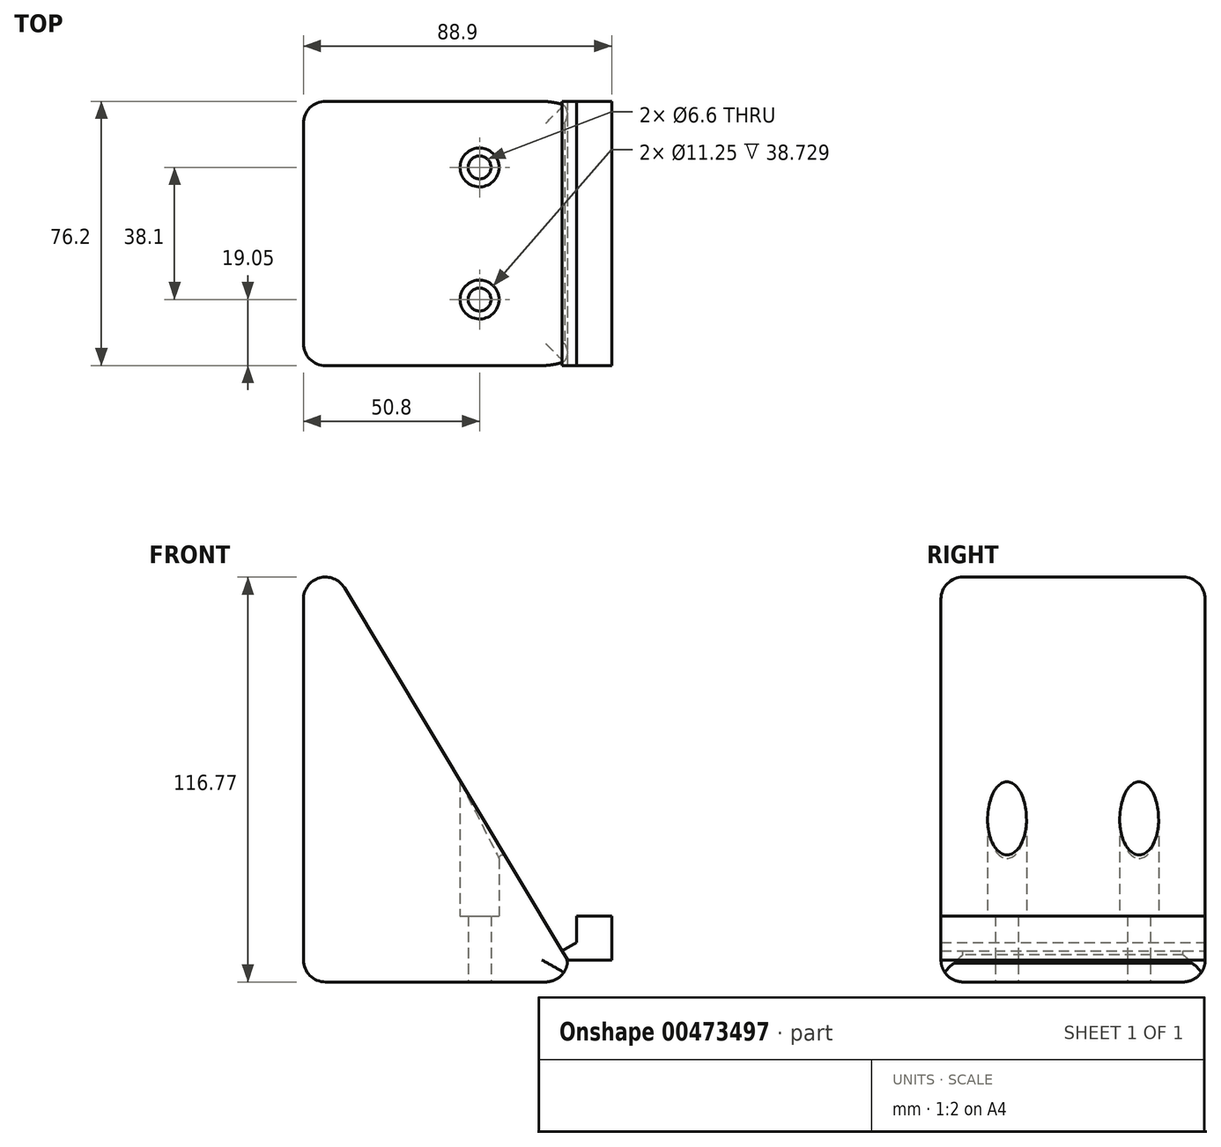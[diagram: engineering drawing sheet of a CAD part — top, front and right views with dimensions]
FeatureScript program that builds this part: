
annotation { "Feature Type Name" : "Feature", "Feature Type Description" : "" }
export const myFeature = defineFeature(function(context is Context, id is Id, definition is map)
    precondition{}
    {
        {
            var Q0;
            Q0=qCreatedBy(makeId("Top.planeOp"),FACE);
            var sketch = newSketch(context, id + "F0", { "sketchPlane" : qUnion([Q0])});
            skLineSegment(sketch, "E0.bottom", {"start": v(-38.1, 38.1) * mm, "end": v(38.1, 38.1) * mm});
            skLineSegment(sketch, "E0.top", {"start": v(-38.1, -38.1) * mm, "end": v(38.1, -38.1) * mm});
            skLineSegment(sketch, "E0.left", {"start": v(-38.1, 38.1) * mm, "end": v(-38.1, -38.1) * mm});
            skLineSegment(sketch, "E0.right", {"start": v(38.1, 38.1) * mm, "end": v(38.1, -38.1) * mm});
            skPoint(sketch, "E0.middle", {"position": v(0, 0) * mm});
            skSolve(sketch);
        }
        {
            var Q0;
            Q0=makeQuery(id+"F0.imprint","IMPRINT",FACE,{"disambiguationData":[TD([[makeQuery(id+"F0.imprint","IMPRINT",EDGE,{"derivedFrom":sQuery(id+"F0.wireOp",EDGE,"E0.bottom")}),-1.0]])]});
            extrude(context, id + "F1", {"entities" : qUnion([Q0]), "oppositeDirection" : true, "depth" : 6.35 * mm});
        }
        {
            var Q0;
            Q0=qCreatedBy(makeId("Front.planeOp"),FACE);
            var sketch = newSketch(context, id + "F2", { "sketchPlane" : qUnion([Q0])});
            skLineSegment(sketch, "E1", {"start": v(38.1, 0) * mm, "end": v(-38.1, 0) * mm});
            skLineSegment(sketch, "E2", {"start": v(38.1, 0) * mm, "end": v(-38.1, 127) * mm});
            skLineSegment(sketch, "E3", {"start": v(-38.1, 127) * mm, "end": v(-38.1, 0) * mm});
            skLineSegment(sketch, "E4", {"start": v(38.1, 0) * mm, "end": v(50.8, 0) * mm});
            skLineSegment(sketch, "E5", {"start": v(50.8, 0) * mm, "end": v(50.8, 12.7) * mm});
            skLineSegment(sketch, "E6", {"start": v(50.8, 12.7) * mm, "end": v(40.64, 12.7) * mm});
            skLineSegment(sketch, "E7", {"start": v(40.64, 12.7) * mm, "end": v(40.64, 5.08) * mm});
            skLineSegment(sketch, "E8", {"start": v(40.64, 5.08) * mm, "end": v(36.53, 2.61) * mm});
            skSolve(sketch);
        }
        {
            var Q0;
            Q0=makeQuery(id+"F2.imprint","IMPRINT",FACE,{"disambiguationData":[TD([[makeQuery(id+"F2.imprint","IMPRINT",EDGE,{"derivedFrom":sQuery(id+"F2.wireOp",EDGE,"E1")}),-1.0]])]});
            extrude(context, id + "F3", {"entities" : qUnion([Q0]), "operationType" : NewBodyOperationType.ADD, "depth" : 38.1 * mm, "hasSecondDirection" : true, "secondDirectionOppositeDirection" : true, "secondDirectionDepth" : 38.1 * mm});
        }
        {
            var Q0;
            Q0=makeQuery(id+"F3.opExtrude","SWEPT_FACE",FACE,{"disambiguationData":[OSD([sQuery(id+"F2.wireOp",EDGE,"E2")])]});
            var Q1;
            Q1=makeQuery(id+"F3.boolean.opBoolean","MERGE",FACE,{"derivedFrom":[makeQuery(id+"F1.opExtrude","SWEPT_FACE",FACE,{"disambiguationData":[OSD([sQuery(id+"F0.wireOp",EDGE,"E0.left")])]}),makeQuery(id+"F3.opExtrude","SWEPT_FACE",FACE,{"disambiguationData":[OSD([sQuery(id+"F2.wireOp",EDGE,"E3")])]})]});
            var Q2;
            Q2=makeQuery(id+"F1.opExtrude","CAP_FACE",FACE,{"disambiguationData":[OSD([sQuery(id+"F0.wireOp",EDGE,"E0.bottom"),sQuery(id+"F0.wireOp",EDGE,"E0.top"),sQuery(id+"F0.wireOp",EDGE,"E0.left"),sQuery(id+"F0.wireOp",EDGE,"E0.right")])],"isStart":false});
            fillet(context, id + "F4", {"entities" : qUnion([Q0, Q1, Q2]), "radius" : 6.35 * mm, "tangentPropagation" : true, "allowEdgeOverflow" : false});
        }
        {
            var Q0;
            Q0=makeQuery(id+"F1.opExtrude","CAP_FACE",FACE,{"disambiguationData":[OSD([sQuery(id+"F0.wireOp",EDGE,"E0.bottom"),sQuery(id+"F0.wireOp",EDGE,"E0.top"),sQuery(id+"F0.wireOp",EDGE,"E0.left"),sQuery(id+"F0.wireOp",EDGE,"E0.right")])],"isStart":false});
            var sketch = newSketch(context, id + "F5", { "sketchPlane" : qUnion([Q0])});
            skLineSegment(sketch, "E9", {"start": v(0, 0) * mm, "end": v(12.7, 0) * mm});
            skLineSegment(sketch, "E10", {"start": v(12.7, 0) * mm, "end": v(12.7, -19.05) * mm});
            skLineSegment(sketch, "E11", {"start": v(12.7, 0) * mm, "end": v(12.7, 19.05) * mm});
            skCircle(sketch, "E12", {"center": v(12.7, -19.05) * mm, "radius": 3.3 * mm});
            skCircle(sketch, "E13", {"center": v(12.7, 19.05) * mm, "radius": 3.3 * mm});
            skCircle(sketch, "E14", {"center": v(12.7, -19.05) * mm, "radius": 5.63 * mm});
            skCircle(sketch, "E15", {"center": v(12.7, 19.05) * mm, "radius": 5.63 * mm});
            skSolve(sketch);
        }
        {
            var Q0;
            Q0=makeQuery(id+"F5.imprint","IMPRINT",FACE,{"disambiguationData":[TD([[makeQuery(id+"F5.imprint","IMPRINT",EDGE,{"derivedFrom":sQuery(id+"F5.wireOp",EDGE,"E13")}),1.0]])]});
            var Q1;
            Q1=makeQuery(id+"F5.imprint","IMPRINT",FACE,{"disambiguationData":[TD([[makeQuery(id+"F5.imprint","IMPRINT",EDGE,{"derivedFrom":sQuery(id+"F5.wireOp",EDGE,"E12")}),1.0]])]});
            extrude(context, id + "F6", {"entities" : qUnion([Q0, Q1]), "operationType" : NewBodyOperationType.REMOVE, "endBound" : BoundingType.THROUGH_ALL, "oppositeDirection" : true, "depth" : 25.4 * mm});
        }
        {
            var Q0;
            Q0=makeQuery(id+"F5.imprint","IMPRINT",FACE,{"disambiguationData":[TD([[makeQuery(id+"F5.imprint","IMPRINT",EDGE,{"derivedFrom":sQuery(id+"F5.wireOp",EDGE,"E13")}),-1.0]])]});
            var Q1;
            Q1=makeQuery(id+"F5.imprint","IMPRINT",FACE,{"disambiguationData":[TD([[makeQuery(id+"F5.imprint","IMPRINT",EDGE,{"derivedFrom":sQuery(id+"F5.wireOp",EDGE,"E12")}),-1.0]])]});
            extrude(context, id + "F7", {"entities" : qUnion([Q0, Q1]), "operationType" : NewBodyOperationType.REMOVE, "endBound" : BoundingType.THROUGH_ALL, "oppositeDirection" : true, "depth" : 76.2 * mm, "hasSecondDirection" : true, "secondDirectionOppositeDirection" : true, "secondDirectionDepth" : 19.05 * mm});
        }
        {
            var Q0;
            Q0=makeQuery(id+"F7.boolean.opBoolean","INTERSECT",EDGE,{"derivedFrom":[makeQuery(id+"F3.opExtrude","SWEPT_FACE",FACE,{"disambiguationData":[OSD([sQuery(id+"F2.wireOp",EDGE,"E2")])]}),makeQuery(id+"F7.opExtrude","SWEPT_FACE",FACE,{"disambiguationData":[OSD([sQuery(id+"F5.wireOp",EDGE,"E15")])]})]});
            var Q1;
            Q1=makeQuery(id+"F7.boolean.opBoolean","INTERSECT",EDGE,{"derivedFrom":[makeQuery(id+"F3.opExtrude","SWEPT_FACE",FACE,{"disambiguationData":[OSD([sQuery(id+"F2.wireOp",EDGE,"E2")])]}),makeQuery(id+"F7.opExtrude","SWEPT_FACE",FACE,{"disambiguationData":[OSD([sQuery(id+"F5.wireOp",EDGE,"E14")])]})]});
            var Q2;
            Q2=makeQuery(id+"F7.boolean.opBoolean","COPY",EDGE,{"derivedFrom":makeQuery(id+"F7.opExtrude","CAP_EDGE",EDGE,{"disambiguationData":[OSD([sQuery(id+"F5.wireOp",EDGE,"E13")])],"isStart":true})});
            var Q3;
            Q3=makeQuery(id+"F7.boolean.opBoolean","COPY",EDGE,{"derivedFrom":makeQuery(id+"F7.opExtrude","CAP_EDGE",EDGE,{"disambiguationData":[OSD([sQuery(id+"F5.wireOp",EDGE,"E12")])],"isStart":true})});
            var Q4;
            Q4=makeQuery(id+"F6.boolean.opBoolean","COPY",EDGE,{"derivedFrom":makeQuery(id+"F6.opExtrude","CAP_EDGE",EDGE,{"disambiguationData":[OSD([sQuery(id+"F5.wireOp",EDGE,"E13")])],"isStart":true})});
            var Q5;
            Q5=makeQuery(id+"F6.boolean.opBoolean","COPY",EDGE,{"derivedFrom":makeQuery(id+"F6.opExtrude","CAP_EDGE",EDGE,{"disambiguationData":[OSD([sQuery(id+"F5.wireOp",EDGE,"E12")])],"isStart":true})});
            fillet(context, id + "F8", {"entities" : qUnion([Q0, Q1, Q2, Q3, Q4, Q5]), "radius" : 1.02 * mm, "allowEdgeOverflow" : false});
        }
        {
            var Q0;
            {var subQ0=sQuery(id+"F2.wireOp",EDGE,"E4");Q0=makeQuery(id+"F2.imprint","IMPRINT",FACE,{"disambiguationData":[TD([[makeQuery(id+"F2.imprint","IMPRINT",EDGE,{"derivedFrom":subQ0}),1.0]])]});}
            extrude(context, id + "F9", {"entities" : qUnion([Q0]), "operationType" : NewBodyOperationType.ADD, "depth" : 38.1 * mm, "offsetDistance" : 25.4 * mm, "hasSecondDirection" : true, "secondDirectionOppositeDirection" : true, "secondDirectionDepth" : 38.1 * mm});
        }
    });
